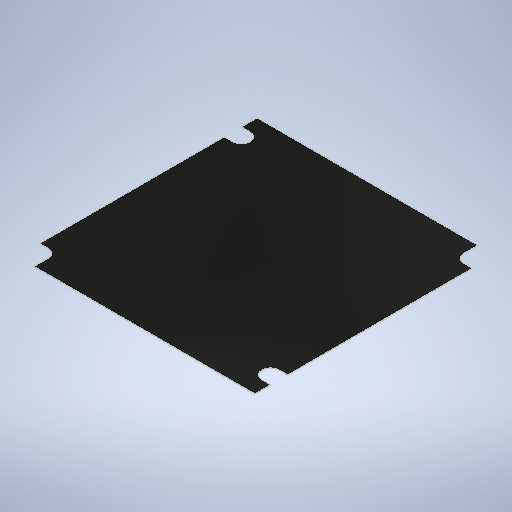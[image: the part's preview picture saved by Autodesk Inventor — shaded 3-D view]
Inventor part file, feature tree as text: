
AUTODESK INVENTOR PART (.ipt)
format: ipt  version: 2025 (Build 290162000, 162)  size: 308,736 bytes
history: native  units: in
note: dims shown in document units (in); Inventor stores cm internally (conversion verified against a paired STEP export)
features: extrude x3, sketch x3
ambient origin geometry x8: Origin, YZ Plane, XZ Plane, XY Plane, X Axis, Y Axis, Z Axis, Center Point
bodies: Solid1 (feature_tree)
feature tree (6):
  extrude  "Extrusion1"  Depth=1.6378in
  extrude  "Extrusion2"  Depth=0.0031in TaperAngle=0.0deg
  extrude  "Extrusion3"  Depth=0.0031in
  sketch  "Sketch2"  dims[d2=0.0031in d3=0.0in d6=0.0031in d7=0.0in]
  sketch  "Sketch Circular Pattern1"  dims[d0=1.6535in d1=1.6378in]
  sketch  "Sketch3"  dims[d16=0.0591in d17=0.1673in d18=0.0591in d20=0.0591in d22=1.5571in d23=0.8268in d24=1.6535in d25=1.6378in d26=0.8189in d27=0.7874in d29=360.0deg d31=0.0031in d32=0.0in]
